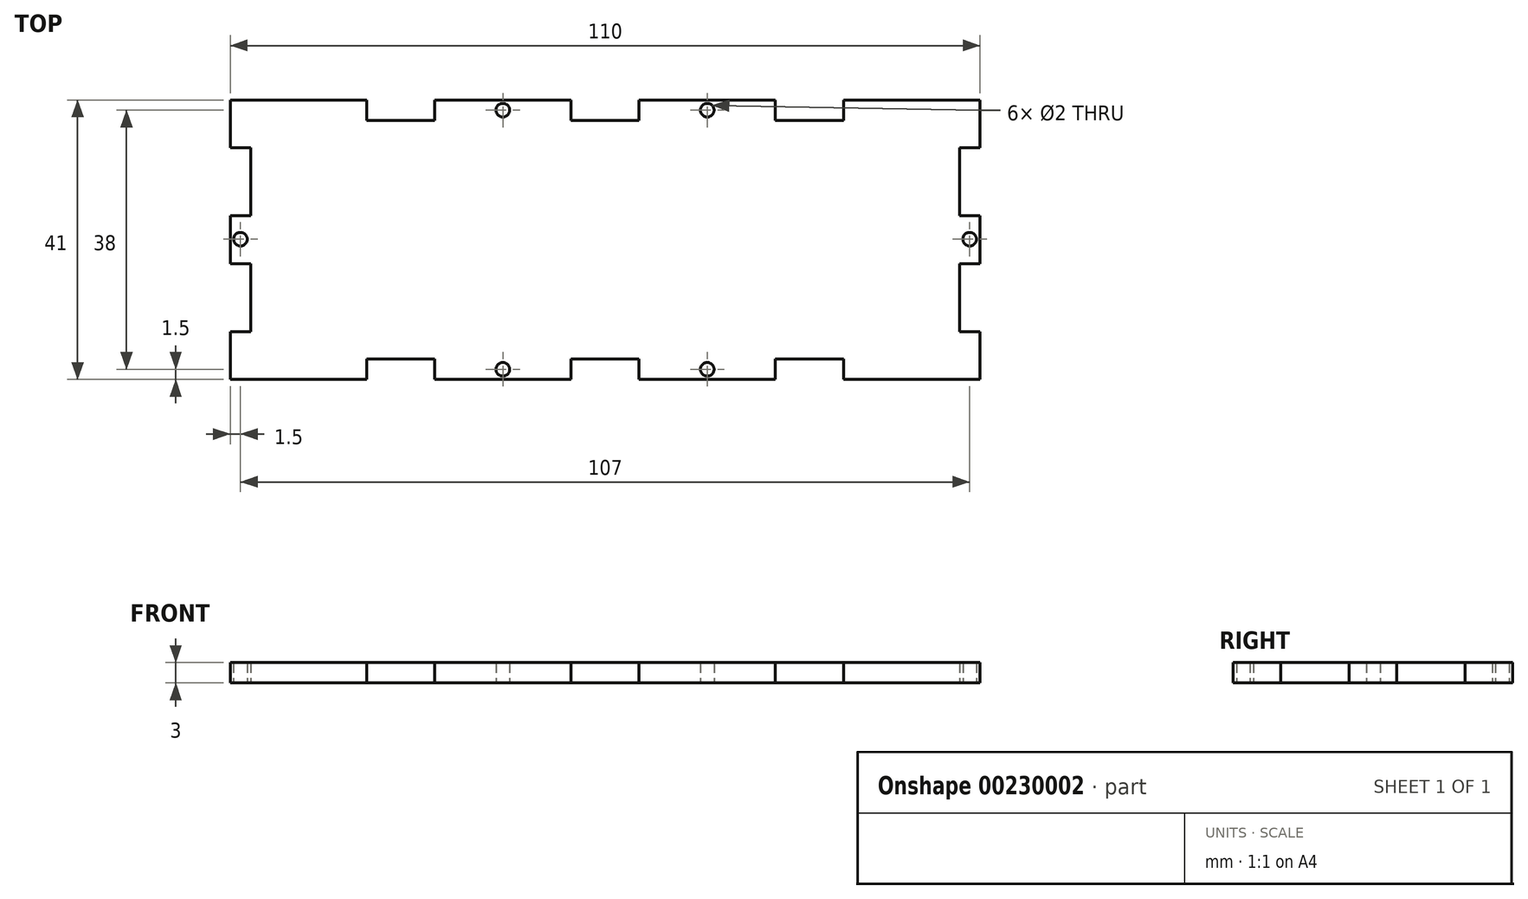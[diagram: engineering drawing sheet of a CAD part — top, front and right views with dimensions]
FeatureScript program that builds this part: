
annotation { "Feature Type Name" : "Feature", "Feature Type Description" : "" }
export const myFeature = defineFeature(function(context is Context, id is Id, definition is map)
    precondition{}
    {
        {
            var Q0;
            Q0=qCreatedBy(makeId("Top.planeOp"),FACE);
            var sketch = newSketch(context, id + "F0", { "sketchPlane" : qUnion([Q0])});
            skLineSegment(sketch, "E0", {"start": v(0, 0) * mm, "end": v(0, 7) * mm});
            skLineSegment(sketch, "E1", {"start": v(0, 7) * mm, "end": v(3, 7) * mm});
            skLineSegment(sketch, "E2", {"start": v(3, 7) * mm, "end": v(3, 17) * mm});
            skLineSegment(sketch, "E3", {"start": v(3, 17) * mm, "end": v(0, 17) * mm});
            skLineSegment(sketch, "E4", {"start": v(0, 17) * mm, "end": v(0, 24) * mm});
            skLineSegment(sketch, "E5", {"start": v(0, 24) * mm, "end": v(3, 24) * mm});
            skLineSegment(sketch, "E6", {"start": v(3, 24) * mm, "end": v(3, 34) * mm});
            skLineSegment(sketch, "E7", {"start": v(3, 34) * mm, "end": v(0, 34) * mm});
            skLineSegment(sketch, "E8", {"start": v(0, 34) * mm, "end": v(0, 41) * mm});
            skLineSegment(sketch, "E9", {"start": v(0, 41) * mm, "end": v(20, 41) * mm});
            skLineSegment(sketch, "E10", {"start": v(20, 41) * mm, "end": v(20, 38) * mm});
            skLineSegment(sketch, "E11", {"start": v(20, 38) * mm, "end": v(30, 38) * mm});
            skLineSegment(sketch, "E12", {"start": v(30, 38) * mm, "end": v(30, 41) * mm});
            skLineSegment(sketch, "E13", {"start": v(30, 41) * mm, "end": v(50, 41) * mm});
            skLineSegment(sketch, "E14", {"start": v(50, 41) * mm, "end": v(50, 38) * mm});
            skLineSegment(sketch, "E15", {"start": v(50, 38) * mm, "end": v(55, 38) * mm});
            skLineSegment(sketch, "E16", {"start": v(0, 0) * mm, "end": v(20, 0) * mm});
            skLineSegment(sketch, "E17", {"start": v(20, 0) * mm, "end": v(20, 3) * mm});
            skLineSegment(sketch, "E18", {"start": v(20, 3) * mm, "end": v(30, 3) * mm});
            skLineSegment(sketch, "E19", {"start": v(30, 3) * mm, "end": v(30, 0) * mm});
            skLineSegment(sketch, "E20", {"start": v(30, 0) * mm, "end": v(50, 0) * mm});
            skLineSegment(sketch, "E21", {"start": v(50, 0) * mm, "end": v(50, 3) * mm});
            skLineSegment(sketch, "E22", {"start": v(50, 3) * mm, "end": v(55, 3) * mm});
            skLineSegment(sketch, "E23.MirrorCS", {"start": v(110, 7) * mm, "end": v(107, 7) * mm});
            skLineSegment(sketch, "E24.MirrorCS", {"start": v(107, 17) * mm, "end": v(110, 17) * mm});
            skLineSegment(sketch, "E25.MirrorCS", {"start": v(107, 34) * mm, "end": v(110, 34) * mm});
            skLineSegment(sketch, "E26.MirrorCS", {"start": v(110, 24) * mm, "end": v(107, 24) * mm});
            skLineSegment(sketch, "E27.MirrorCS", {"start": v(80, 3) * mm, "end": v(80, 0) * mm});
            skLineSegment(sketch, "E28.MirrorCS", {"start": v(60, 0) * mm, "end": v(60, 3) * mm});
            skLineSegment(sketch, "E29.MirrorCS", {"start": v(90, 41) * mm, "end": v(90, 38) * mm});
            skLineSegment(sketch, "E30.MirrorCS", {"start": v(60, 41) * mm, "end": v(60, 38) * mm});
            skLineSegment(sketch, "E31.MirrorCS", {"start": v(90, 0) * mm, "end": v(90, 3) * mm});
            skLineSegment(sketch, "E32.MirrorCS", {"start": v(80, 38) * mm, "end": v(80, 41) * mm});
            skLineSegment(sketch, "E33.MirrorCS", {"start": v(110, 0) * mm, "end": v(110, 7) * mm});
            skLineSegment(sketch, "E34.MirrorCS", {"start": v(107, 7) * mm, "end": v(107, 17) * mm});
            skLineSegment(sketch, "E35.MirrorCS", {"start": v(110, 34) * mm, "end": v(110, 41) * mm});
            skLineSegment(sketch, "E36.MirrorCS", {"start": v(110, 0) * mm, "end": v(90, 0) * mm});
            skLineSegment(sketch, "E37.MirrorCS", {"start": v(90, 3) * mm, "end": v(80, 3) * mm});
            skLineSegment(sketch, "E38.MirrorCS", {"start": v(60, 3) * mm, "end": v(55, 3) * mm});
            skLineSegment(sketch, "E39.MirrorCS", {"start": v(80, 0) * mm, "end": v(60, 0) * mm});
            skLineSegment(sketch, "E40.MirrorCS", {"start": v(107, 24) * mm, "end": v(107, 34) * mm});
            skLineSegment(sketch, "E41.MirrorCS", {"start": v(110, 17) * mm, "end": v(110, 24) * mm});
            skLineSegment(sketch, "E42.MirrorCS", {"start": v(110, 41) * mm, "end": v(90, 41) * mm});
            skLineSegment(sketch, "E43.MirrorCS", {"start": v(80, 41) * mm, "end": v(60, 41) * mm});
            skLineSegment(sketch, "E44.MirrorCS", {"start": v(60, 38) * mm, "end": v(55, 38) * mm});
            skLineSegment(sketch, "E45.MirrorCS", {"start": v(90, 38) * mm, "end": v(80, 38) * mm});
            skCircle(sketch, "E46", {"center": v(40, 39.5) * mm, "radius": 1 * mm});
            skPoint(sketch, "E46.centerSnap0", {"position": v(40, 41) * mm});
            skCircle(sketch, "E47.MirrorC", {"center": v(70, 39.5) * mm, "radius": 1 * mm});
            skCircle(sketch, "E48.MirrorC", {"center": v(40, 1.5) * mm, "radius": 1 * mm});
            skCircle(sketch, "E49.MirrorC", {"center": v(70, 1.5) * mm, "radius": 1 * mm});
            skCircle(sketch, "E50.MirrorC", {"center": v(1.5, 20.58) * mm, "radius": 1 * mm});
            skCircle(sketch, "E51.MirrorC", {"center": v(108.5, 20.58) * mm, "radius": 1 * mm});
            skPoint(sketch, "E52", {"position": v(3, 29) * mm});
            skSolve(sketch);
        }
        {
            var Q0;
            Q0=qSketchRegion(id+"F0",true);
            extrude(context, id + "F1", {"entities" : qUnion([Q0]), "depth" : 3 * mm});
        }
    });
